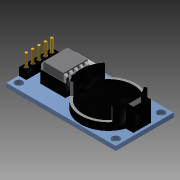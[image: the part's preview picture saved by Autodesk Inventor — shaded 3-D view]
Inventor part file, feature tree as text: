
AUTODESK INVENTOR PART (.ipt)
format: ipt  version: 2014 SP1 (Build 180222100, 222)  size: 456,704 bytes
history: native  units: mm
features: extrude x14, sketch x14, fillet x2, projected_geometry x2
ambient origin geometry x8: Origin, YZ Plane, XZ Plane, XY Plane, X Axis, Y Axis, Z Axis, Center Point
bodies: Body1 (feature_tree)
feature tree (32):
  extrude  "Выдавливание2"  Depth=43.5mm
  extrude  "Выдавливание3"  Depth=23.0mm
  extrude  "Выдавливание4"  Depth=38.5mm
  extrude  "Выдавливание5"  Depth=3.0mm
  extrude  "Выдавливание6"  Depth=3.0mm
  extrude  "Выдавливание7"  Depth=38.5mm
  extrude  "Выдавливание8"  Depth=18.0mm
  extrude  "Выдавливание9"  Depth=18.0mm
  fillet  "Сопряжение1"  Radius=2.5mm
  extrude  "Выдавливание10"  Depth=2.5mm
  extrude  "Выдавливание11"  Depth=2.5mm
  extrude  "Выдавливание12"  Depth=2.5mm
  extrude  "Выдавливание13"  Depth=1.7mm TaperAngle=0.0deg
  extrude  "Выдавливание14"  Depth=22.0mm
  fillet  "Сопряжение2"  Radius=8.0mm
  extrude  "Выдавливание15"  Depth=8.0mm
  sketch  "Эскиз1"
  sketch  "Эскиз2"
  sketch  "Эскиз3"
  sketch  "Эскиз4"
  sketch  "Эскиз5"
  sketch  "Эскиз6"
  sketch  "Эскиз7"
  sketch  "Эскиз8"
  projected_geometry  "Спроецированная петля1"
  sketch  "Эскиз9"
  sketch  "Эскиз10"
  sketch  "Эскиз11"
  projected_geometry  "Спроецированная петля2"
  sketch  "Эскиз12"
  sketch  "Эскиз13"
  sketch  "Эскиз14"
